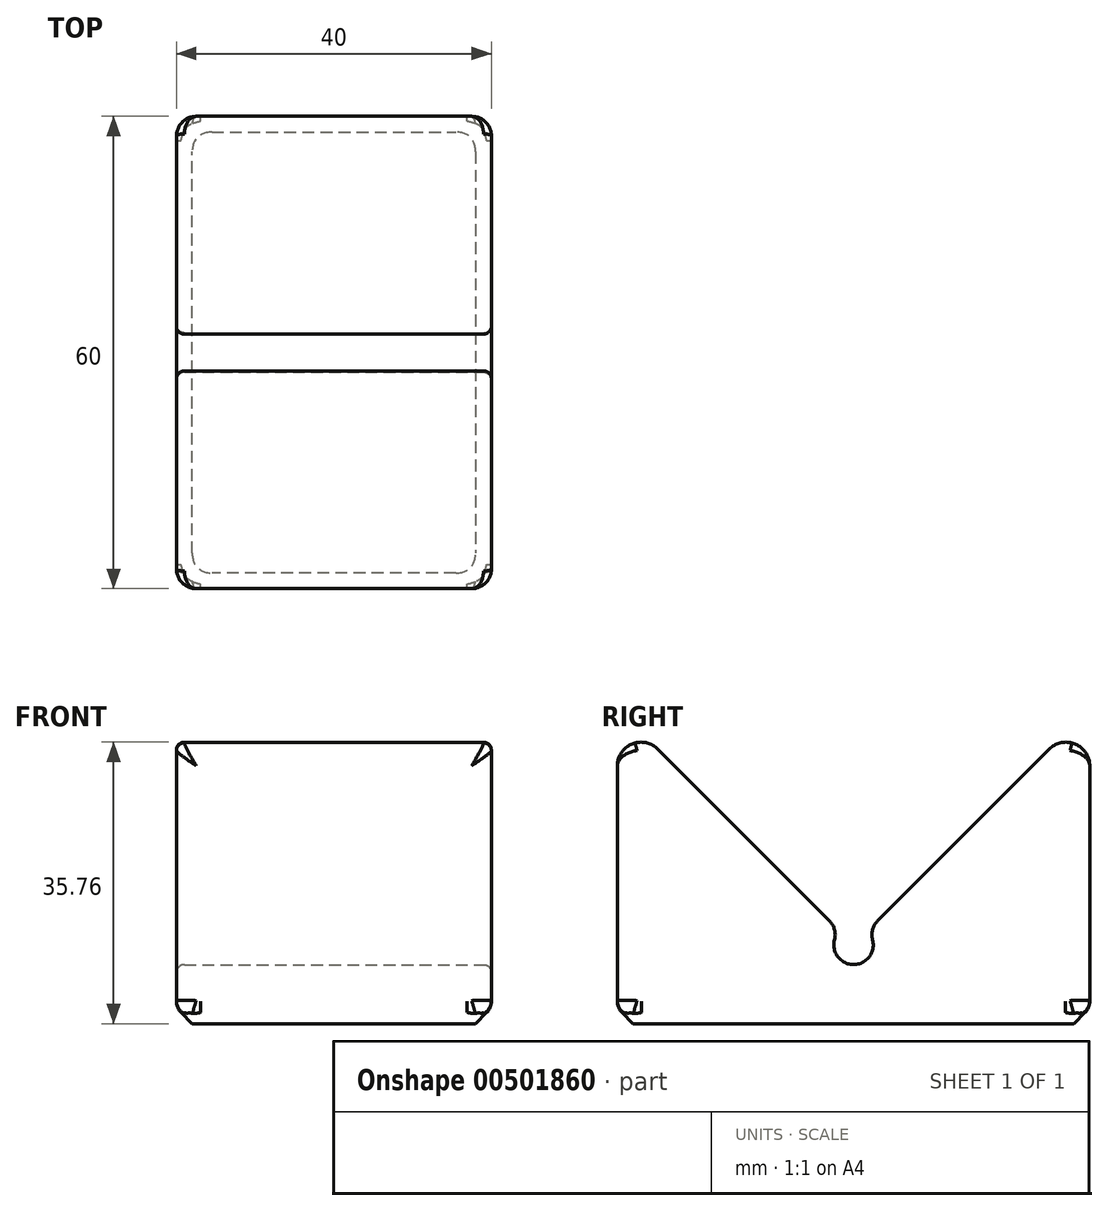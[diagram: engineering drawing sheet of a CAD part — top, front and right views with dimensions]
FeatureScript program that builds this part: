
annotation { "Feature Type Name" : "Feature", "Feature Type Description" : "" }
export const myFeature = defineFeature(function(context is Context, id is Id, definition is map)
    precondition{}
    {
        {
            assignVariable(context, id + "F0", {"name" : "length", "anyValue" : 40});
        }
        {
            assignVariable(context, id + "F1", {"name" : "width", "anyValue" : 60});
        }
        {
            var Q0;
            Q0=qCreatedBy(makeId("Top.planeOp"),FACE);
            var sketch = newSketch(context, id + "F2", { "sketchPlane" : qUnion([Q0])});
            skLineSegment(sketch, "E0.bottom", {"start": v(-72.8, -31.56) * mm, "end": v(-32.8, -31.56) * mm});
            skLineSegment(sketch, "E0.top", {"start": v(-72.8, 28.44) * mm, "end": v(-32.8, 28.44) * mm});
            skLineSegment(sketch, "E0.left", {"start": v(-72.8, -31.56) * mm, "end": v(-72.8, 28.44) * mm});
            skLineSegment(sketch, "E0.right", {"start": v(-32.8, -31.56) * mm, "end": v(-32.8, 28.44) * mm});
            skLineSegment(sketch, "E1.bottom", {"start": v(-63.73, 28.44) * mm, "end": v(-43.02, 28.44) * mm});
            skLineSegment(sketch, "E1.top", {"start": v(-63.73, 7.5) * mm, "end": v(-43.02, 7.5) * mm});
            skLineSegment(sketch, "E1.left", {"start": v(-63.73, 28.44) * mm, "end": v(-63.73, 7.5) * mm});
            skLineSegment(sketch, "E1.right", {"start": v(-43.02, 28.44) * mm, "end": v(-43.02, 7.5) * mm});
            skLineSegment(sketch, "E2.bottom", {"start": v(-65.71, -31.56) * mm, "end": v(-41.22, -31.56) * mm});
            skLineSegment(sketch, "E2.top", {"start": v(-65.71, -14.98) * mm, "end": v(-41.22, -14.98) * mm});
            skLineSegment(sketch, "E2.left", {"start": v(-65.71, -31.56) * mm, "end": v(-65.71, -14.98) * mm});
            skLineSegment(sketch, "E2.right", {"start": v(-41.22, -31.56) * mm, "end": v(-41.22, -14.98) * mm});
            skSolve(sketch);
        }
        {
            var Q0;
            Q0=qSketchRegion(id+"F2",true);
            extrude(context, id + "F3", {"entities" : qUnion([Q0]), "depth" : (getVariable(context, 'width')) * mm, "offsetDistance" : 25 * mm});
        }
        {
            var Q0;
            Q0=makeQuery(id+"F3.opExtrude","SWEPT_FACE",FACE,{"disambiguationData":[OSD([sQuery(id+"F2.wireOp",EDGE,"E0.right")])]});
            var sketch = newSketch(context, id + "F4", { "sketchPlane" : qUnion([Q0])});
            skLineSegment(sketch, "E3.bottom", {"start": v(-52.47, 60.91) * mm, "end": v(-4.62, 13.06) * mm});
            skLineSegment(sketch, "E3.top", {"start": v(-1.56, 111.82) * mm, "end": v(49.35, 60.91) * mm});
            skLineSegment(sketch, "E3.left", {"start": v(-52.47, 60.91) * mm, "end": v(-1.56, 111.82) * mm});
            skLineSegment(sketch, "E3.right", {"start": v(1.5, 13.06) * mm, "end": v(49.35, 60.91) * mm});
            skPoint(sketch, "E3.middle", {"position": v(-1.56, 60.91) * mm});
            skLineSegment(sketch, "E4", {"start": v(-31.56, 10) * mm, "end": v(28.44, 10) * mm, "construction": true});
            skArc(sketch, "E5", {"start": v(-3.97, 10.65) * mm, "mid": v(-1.56, 7.5) * mm, "end": v(0.86, 10.65) * mm});
            skPoint(sketch, "E6.visualSharp", {"position": v(-3.33, 11.77) * mm});
            skArc(sketch, "E6.filletArc", {"start": v(-3.97, 10.65) * mm, "mid": v(-3.97, 11.94) * mm, "end": v(-4.62, 13.06) * mm});
            skPoint(sketch, "E7.visualSharp", {"position": v(0.21, 11.77) * mm});
            skArc(sketch, "E7.filletArc", {"start": v(1.5, 13.06) * mm, "mid": v(0.86, 11.94) * mm, "end": v(0.86, 10.65) * mm});
            skSolve(sketch);
        }
        {
            var Q0;
            Q0=qSketchRegion(id+"F4",true);
            extrude(context, id + "F5", {"entities" : qUnion([Q0]), "operationType" : NewBodyOperationType.REMOVE, "oppositeDirection" : true, "depth" : (getVariable(context, 'length')) * mm});
        }
        {
            var Q0;
            Q0=makeQuery(id+"F3.opExtrude","CAP_FACE",FACE,{"disambiguationData":[OSD([sQuery(id+"F2.wireOp",EDGE,"E0.bottom"),sQuery(id+"F2.wireOp",EDGE,"E0.top"),sQuery(id+"F2.wireOp",EDGE,"E0.left"),sQuery(id+"F2.wireOp",EDGE,"E0.right")])],"isStart":true});
            chamfer(context, id + "F6", {"entities" : qUnion([Q0]), "width" : 2 * mm, "tangentPropagation" : true});
        }
        {
            var Q0;
            Q0=makeQuery(id+"F5.boolean.opBoolean","INTERSECT",EDGE,{"derivedFrom":[makeQuery(id+"F3.opExtrude","SWEPT_FACE",FACE,{"disambiguationData":[OSD([sQuery(id+"F2.wireOp",EDGE,"E0.bottom")])]}),makeQuery(id+"F5.opExtrude","SWEPT_FACE",FACE,{"disambiguationData":[OSD([sQuery(id+"F4.wireOp",EDGE,"E3.bottom")])]})]});
            var Q1;
            Q1=makeQuery(id+"F5.boolean.opBoolean","INTERSECT",EDGE,{"derivedFrom":[makeQuery(id+"F3.opExtrude","SWEPT_FACE",FACE,{"disambiguationData":[OSD([sQuery(id+"F2.wireOp",EDGE,"E0.top")])]}),makeQuery(id+"F5.opExtrude","SWEPT_FACE",FACE,{"disambiguationData":[OSD([sQuery(id+"F4.wireOp",EDGE,"E3.right")])]})]});
            fillet(context, id + "F7", {"entities" : qUnion([Q0, Q1]), "radius" : 3 * mm, "tangentPropagation" : true, "allowEdgeOverflow" : false});
        }
        {
            var Q0;
            Q0=makeQuery(id+"F3.opExtrude","SWEPT_EDGE",EDGE,{"disambiguationData":[OSD([sQuery(id+"F2.wireOp",EDGE,"E0.bottom"),sQuery(id+"F2.wireOp",EDGE,"E0.right")])]});
            var Q1;
            Q1=makeQuery(id+"F3.opExtrude","SWEPT_EDGE",EDGE,{"disambiguationData":[OSD([sQuery(id+"F2.wireOp",EDGE,"E0.top"),sQuery(id+"F2.wireOp",EDGE,"E0.right")])]});
            var Q2;
            Q2=makeQuery(id+"F3.opExtrude","SWEPT_EDGE",EDGE,{"disambiguationData":[OSD([sQuery(id+"F2.wireOp",EDGE,"E0.bottom"),sQuery(id+"F2.wireOp",EDGE,"E0.left")])]});
            var Q3;
            Q3=makeQuery(id+"F3.opExtrude","SWEPT_EDGE",EDGE,{"disambiguationData":[OSD([sQuery(id+"F2.wireOp",EDGE,"E0.top"),sQuery(id+"F2.wireOp",EDGE,"E0.left")])]});
            fillet(context, id + "F8", {"entities" : qUnion([Q0, Q1, Q2, Q3]), "radius" : 2.5 * mm, "allowEdgeOverflow" : false});
        }
        {
            var Q0;
            Q0=makeQuery(id+"F6.opChamfer","BLEND_EDGE",EDGE,{"blendedFrom":[makeQuery(id+"F3.opExtrude","CAP_EDGE",EDGE,{"disambiguationData":[OSD([sQuery(id+"F2.wireOp",EDGE,"E0.top")])],"isStart":true}),makeQuery(id+"F3.opExtrude","CAP_EDGE",EDGE,{"disambiguationData":[OSD([sQuery(id+"F2.wireOp",EDGE,"E0.left")])],"isStart":true})],"blendedInto":[]});
            var Q1;
            Q1=makeQuery(id+"F6.opChamfer","BLEND_EDGE",EDGE,{"blendedFrom":[makeQuery(id+"F3.opExtrude","CAP_EDGE",EDGE,{"disambiguationData":[OSD([sQuery(id+"F2.wireOp",EDGE,"E0.bottom")])],"isStart":true}),makeQuery(id+"F3.opExtrude","CAP_EDGE",EDGE,{"disambiguationData":[OSD([sQuery(id+"F2.wireOp",EDGE,"E0.left")])],"isStart":true})],"blendedInto":[]});
            var Q2;
            Q2=makeQuery(id+"F6.opChamfer","BLEND_EDGE",EDGE,{"blendedFrom":[makeQuery(id+"F3.opExtrude","CAP_EDGE",EDGE,{"disambiguationData":[OSD([sQuery(id+"F2.wireOp",EDGE,"E0.bottom")])],"isStart":true}),makeQuery(id+"F3.opExtrude","CAP_EDGE",EDGE,{"disambiguationData":[OSD([sQuery(id+"F2.wireOp",EDGE,"E0.right")])],"isStart":true})],"blendedInto":[]});
            var Q3;
            Q3=makeQuery(id+"F6.opChamfer","BLEND_EDGE",EDGE,{"blendedFrom":[makeQuery(id+"F3.opExtrude","CAP_EDGE",EDGE,{"disambiguationData":[OSD([sQuery(id+"F2.wireOp",EDGE,"E0.top")])],"isStart":true}),makeQuery(id+"F3.opExtrude","CAP_EDGE",EDGE,{"disambiguationData":[OSD([sQuery(id+"F2.wireOp",EDGE,"E0.right")])],"isStart":true})],"blendedInto":[]});
            fillet(context, id + "F9", {"entities" : qUnion([Q0, Q1, Q2, Q3]), "radius" : (2.5 * sqrt(2)) * mm, "tangentPropagation" : true, "allowEdgeOverflow" : false});
        }
        {
            var Q0;
            {var subQ0=sQuery(id+"F2.wireOp",EDGE,"E0.right");Q0=makeQuery(id+"F6.opChamfer","BLEND_EDGE",EDGE,{"blendedFrom":[makeQuery(id+"F3.opExtrude","CAP_EDGE",EDGE,{"disambiguationData":[OSD([subQ0])],"isStart":true}),makeQuery(id+"F3.opExtrude","SWEPT_FACE",FACE,{"disambiguationData":[OSD([subQ0])]})],"blendedInto":[makeQuery(id+"F3.opExtrude","SWEPT_FACE",FACE,{"disambiguationData":[OSD([subQ0])]})]});}
            fillet(context, id + "F10", {"entities" : qUnion([Q0]), "radius" : 2 * mm, "tangentPropagation" : true, "allowEdgeOverflow" : false});
        }
        {
            var Q0;
            Q0=makeQuery(id+"F3.opExtrude","SWEPT_FACE",FACE,{"disambiguationData":[OSD([sQuery(id+"F2.wireOp",EDGE,"E0.left")])]});
            var Q1;
            Q1=makeQuery(id+"F3.opExtrude","SWEPT_FACE",FACE,{"disambiguationData":[OSD([sQuery(id+"F2.wireOp",EDGE,"E0.right")])]});
            fillet(context, id + "F11", {"entities" : qUnion([Q0, Q1]), "radius" : 1 * mm, "tangentPropagation" : true, "allowEdgeOverflow" : false});
        }
    });
